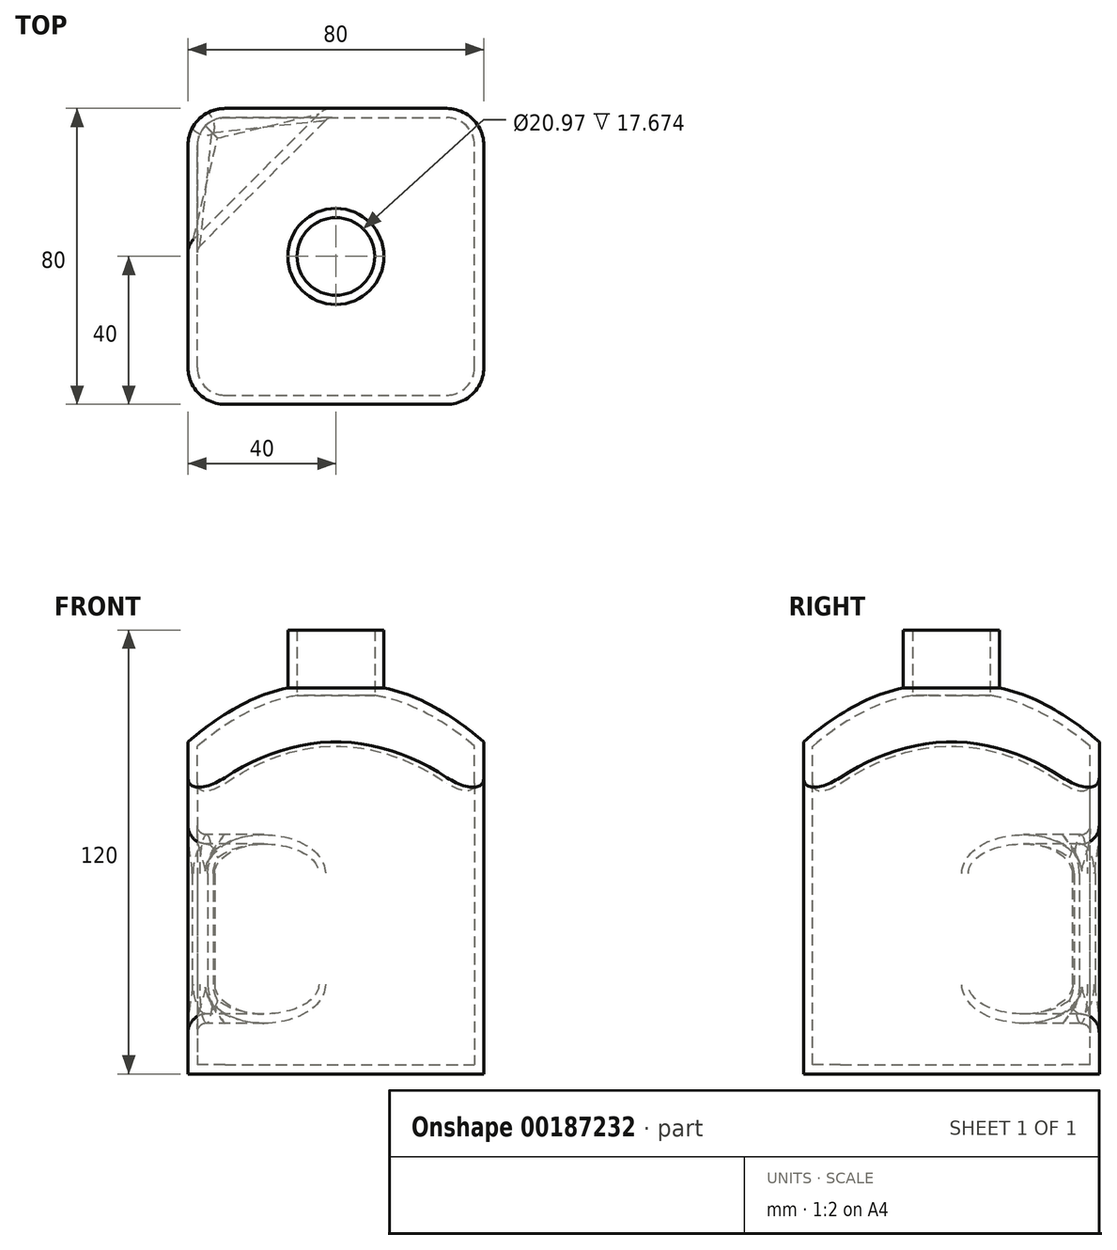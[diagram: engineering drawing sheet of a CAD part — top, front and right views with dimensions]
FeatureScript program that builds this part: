
annotation { "Feature Type Name" : "Feature", "Feature Type Description" : "" }
export const myFeature = defineFeature(function(context is Context, id is Id, definition is map)
    precondition{}
    {
        {
            var Q0;
            Q0=qCreatedBy(makeId("Front.planeOp"),FACE);
            var sketch = newSketch(context, id + "F0", { "sketchPlane" : qUnion([Q0])});
            skLineSegment(sketch, "E0.bottom", {"start": v(-40, 60) * mm, "end": v(40, 60) * mm});
            skLineSegment(sketch, "E0.top", {"start": v(-40, -60) * mm, "end": v(40, -60) * mm});
            skLineSegment(sketch, "E0.left", {"start": v(-40, 60) * mm, "end": v(-40, -60) * mm});
            skLineSegment(sketch, "E0.right", {"start": v(40, 60) * mm, "end": v(40, -60) * mm});
            skPoint(sketch, "E0.middle", {"position": v(0, 0) * mm});
            skSolve(sketch);
        }
        {
            var Q0;
            Q0 = qSketchRegion(id + "F0", true);
            extrude(context, id + "F1", {"entities" : qUnion([Q0]), "endBound" : BoundingType.SYMMETRIC, "depth" : 80 * mm});
        }
        {
            var Q0;
            Q0=qCreatedBy(makeId("Front.planeOp"),FACE);
            var sketch = newSketch(context, id + "F2", { "sketchPlane" : qUnion([Q0])});
            skLineSegment(sketch, "E1", {"start": v(12.99, 61.24) * mm, "end": v(12.99, 44.38) * mm});
            skFitSpline(sketch, "E2", {"points": [v(12.99, 44.38) * mm, v(59.28, 9.2) * mm], "startDerivative": vector(56.93, -11.37) * mm, "endDerivative": vector(29.6, -38.3) * mm});
            skLineSegment(sketch, "E3", {"start": v(0, 60.54) * mm, "end": v(0, 9.2) * mm});
            skLineSegment(sketch, "E4", {"start": v(12.99, 61.24) * mm, "end": v(62.77, 61.24) * mm});
            skLineSegment(sketch, "E5", {"start": v(62.77, 61.24) * mm, "end": v(62.77, 9) * mm});
            skLineSegment(sketch, "E6", {"start": v(62.77, 9) * mm, "end": v(59.28, 9.2) * mm});
            skSolve(sketch);
        }
        {
            var Q0;
            Q0 = qSketchRegion(id + "F2", true);
            var Q1;
            Q1=sQuery(id+"F2.wireOp",EDGE,"E3");
            revolve(context, id + "F3", {"operationType" : NewBodyOperationType.REMOVE, "entities" : qUnion([Q0]), "axis" : qUnion([Q1]), "revolveType" : RevolveType.FULL, "oppositeDirection" : true});
        }
        {
            var Q0;
            Q0=qCreatedBy(makeId("Front.planeOp"),FACE);
            var sketch = newSketch(context, id + "F4", { "sketchPlane" : qUnion([Q0])});
            skLineSegment(sketch, "E7", {"start": v(0, -59.76) * mm, "end": v(0, 29.74) * mm});
            skSolve(sketch);
        }
        {
            var Q0;
            Q0=qCreatedBy(makeId("Right.planeOp"),FACE);
            var Q1;
            Q1=sQuery(id+"F4.wireOp",EDGE,"E7");
            cPlane(context, id + "F5", {"entities" : qUnion([Q0, Q1]), "cplaneType" : CPlaneType.LINE_ANGLE, "offset" : 25 * mm, "angle" : 45 * degree, "width" : 150 * mm, "height" : 150 * mm});
        }
        {
            var Q0;
            Q0=qCreatedBy(id+"F5.planeOp",FACE);
            var sketch = newSketch(context, id + "F6", { "sketchPlane" : qUnion([Q0])});
            skLineSegment(sketch, "E8", {"start": v(-30.5, -5.81) * mm, "end": v(-30.5, -35.81) * mm});
            skArc(sketch, "E9", {"start": v(-30.5, -5.81) * mm, "mid": v(-38.5, 2.19) * mm, "end": v(-46.5, -5.81) * mm});
            skLineSegment(sketch, "E10", {"start": v(-46.5, -5.81) * mm, "end": v(-46.5, -35.81) * mm});
            skArc(sketch, "E11", {"start": v(-46.5, -35.81) * mm, "mid": v(-38.5, -43.81) * mm, "end": v(-30.5, -35.81) * mm});
            skSolve(sketch);
        }
        {
            var Q0;
            Q0 = qSketchRegion(id + "F6", true);
            extrude(context, id + "F7", {"entities" : qUnion([Q0]), "operationType" : NewBodyOperationType.REMOVE, "endBound" : BoundingType.SYMMETRIC, "oppositeDirection" : true, "depth" : 128.4 * mm});
        }
        {
            var Q0;
            Q0=makeQuery(id+"F7.boolean.opBoolean","INTERSECT",EDGE,{"derivedFrom":[makeQuery(id+"F1.opExtrude","CAP_FACE",FACE,{"disambiguationData":[OSD([sQuery(id+"F0.wireOp",EDGE,"E0.bottom"),sQuery(id+"F0.wireOp",EDGE,"E0.top"),sQuery(id+"F0.wireOp",EDGE,"E0.left"),sQuery(id+"F0.wireOp",EDGE,"E0.right")])],"isStart":true}),makeQuery(id+"F7.opExtrude","SWEPT_FACE",FACE,{"disambiguationData":[OSD([sQuery(id+"F6.wireOp",EDGE,"E10")])]})]});
            var Q1;
            Q1=makeQuery(id+"F7.boolean.opBoolean","INTERSECT",EDGE,{"derivedFrom":[makeQuery(id+"F1.opExtrude","SWEPT_FACE",FACE,{"disambiguationData":[OSD([sQuery(id+"F0.wireOp",EDGE,"E0.left")])]}),makeQuery(id+"F7.opExtrude","SWEPT_FACE",FACE,{"disambiguationData":[OSD([sQuery(id+"F6.wireOp",EDGE,"E9")])]})]});
            fillet(context, id + "F8", {"entities" : qUnion([Q0, Q1]), "radius" : 5 * mm, "tangentPropagation" : true, "allowEdgeOverflow" : false});
        }
        {
            var Q0;
            Q0=makeQuery(id+"F1.opExtrude","CAP_EDGE",EDGE,{"disambiguationData":[OSD([sQuery(id+"F0.wireOp",EDGE,"E0.right")])],"isStart":true});
            var Q1;
            Q1=makeQuery(id+"F1.opExtrude","CAP_EDGE",EDGE,{"disambiguationData":[OSD([sQuery(id+"F0.wireOp",EDGE,"E0.right")])],"isStart":false});
            var Q2;
            Q2=makeQuery(id+"F1.opExtrude","CAP_EDGE",EDGE,{"disambiguationData":[OSD([sQuery(id+"F0.wireOp",EDGE,"E0.left")])],"isStart":false});
            var Q3;
            Q3=makeQuery(id+"F1.opExtrude","CAP_EDGE",EDGE,{"disambiguationData":[OSD([sQuery(id+"F0.wireOp",EDGE,"E0.left")])],"isStart":true});
            fillet(context, id + "F9", {"entities" : qUnion([Q0, Q1, Q2, Q3]), "radius" : 10 * mm, "tangentPropagation" : true, "allowEdgeOverflow" : false});
        }
        {
            var Q0;
            Q0=makeQuery(id+"F1.opExtrude","SWEPT_FACE",FACE,{"disambiguationData":[OSD([sQuery(id+"F0.wireOp",EDGE,"E0.bottom")])]});
            shell(context, id + "F10", {"entities" : qUnion([Q0]), "thickness" : 2.5 * mm});
        }
    });
